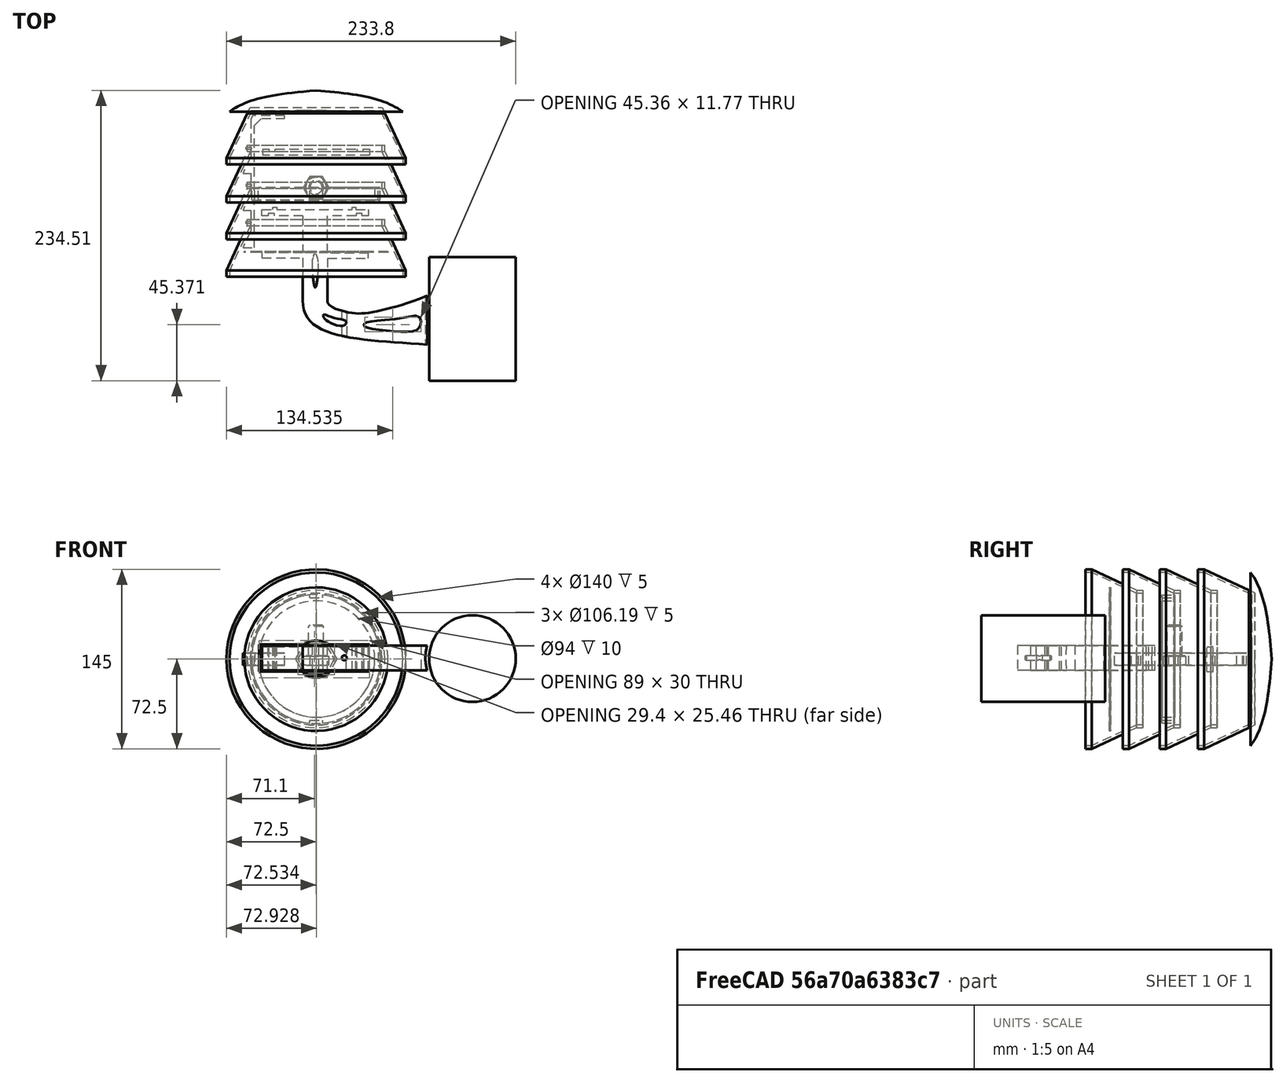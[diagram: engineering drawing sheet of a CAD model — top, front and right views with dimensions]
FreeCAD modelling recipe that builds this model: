
FCSTD DOCUMENT  (FreeCAD 0.21R33771 (Git))
Label: pms7003-external-housing
License: All rights reserved
LicenseURL: http://en.wikipedia.org/wiki/All_rights_reserved
objects: Sketcher::SketchObject×11, Part::Cut×8, Part::Revolution×5, Part::Cylinder×5, Part::Extrusion×5, Part::Box×5, Mesh::Feature×2, App::LinkGroup×2, PartDesign::Body×1, Part::Helix×1, Part::FeaturePython×1, PartDesign::AdditivePipe×1, PartDesign::AdditiveCylinder×1, App::Part×1
note: 46 computed .brp shape members not serialized (recipe doc carries the construction recipe); baked Part::Feature solids carry a one-line shape summary decoded from their .brp

FEATURE [Mesh::Feature] external_v4_case_with_hang_rails  label="external-v4-case-with-hang-rails"
  Placement = pos=(-30.9,-17.3,29) rot=(0,0,1;0rad)
FEATURE [Sketcher::SketchObject] Sketch008
  FullyConstrained = false
  sketch-geometry (8):
    g0: LineSegment StartX=-70 StartY=-1.85789 StartZ=0 EndX=-72.5 EndY=-1.85789 EndZ=0
    g1: LineSegment StartX=-55.5953 StartY=39.3944 StartZ=0 EndX=-55.5953 EndY=44.3944 EndZ=0
    g2: LineSegment StartX=-55.5953 StartY=44.3944 StartZ=0 EndX=-53.0953 EndY=44.3944 EndZ=0
    g3: LineSegment StartX=-53.0953 StartY=39.3944 StartZ=0 EndX=-70 EndY=3.14211 EndZ=0
    g4: LineSegment StartX=-70 StartY=3.14211 StartZ=0 EndX=-70 EndY=-1.85789 EndZ=0
    g5: LineSegment StartX=-72.5 StartY=-1.85789 StartZ=0 EndX=-72.5 EndY=3.14211 EndZ=0
    g6: LineSegment StartX=-72.5 StartY=3.14211 StartZ=0 EndX=-55.5953 EndY=39.3944 EndZ=0
    g7: LineSegment StartX=-53.0953 StartY=44.3944 StartZ=0 EndX=-53.0953 EndY=39.3944 EndZ=0
  constraints (23):
    c: Coincident(g0,g5)
    c: Coincident(g6,g1)
    c: Coincident(g1,g2)
    c: Coincident(g7,g3)
    c: Coincident(g4,g0)
    c: Vertical(g1)
    c: Coincident(g3,g4)
    c: Coincident(g5,g6)
    c: Parallel(g6,g3)
    c: Vertical(g5)
    c: Vertical(g4)
    c: DistanceY(g5,g5) = 5
    c: Distance(g6) = 40
    c: Vertical(g7)
    c: DistanceX(g0,g-1) = 70
    c: Coincident(g7,g2)
    c: DistanceY(g1,g1) = 5
    c: Angle(g-1,g6) = 1.13446
    c: DistanceY(g4,g4) = 5
    c: DistanceY(g7,g7) = 5
    c: Horizontal(g0)
    c: DistanceX(g5,g3) = 2.5
    c: Horizontal(g2)
FEATURE [Part::Revolution] Revolve004  label="ring"
  Angle = 360
  Axis = (0,1,0)
  Base = (0,0,0)
  FaceMakerClass = Part::FaceMakerBullseye
  Placement = pos=(0,-70,0) rot=(0,0,1;0rad)
  Solid = true
  Source = -> Sketch008
  Symmetric = false
FEATURE [Sketcher::SketchObject] Sketch009
  FullyConstrained = false
  sketch-geometry (9):
    g0: LineSegment StartX=-70 StartY=-1.80024 StartZ=0 EndX=-72.5 EndY=-1.80024 EndZ=0
    g1: LineSegment StartX=-52.0979 StartY=41.591 StartZ=0 EndX=-70 EndY=3.19976 EndZ=0
    g2: LineSegment StartX=-70 StartY=3.19976 StartZ=0 EndX=-70 EndY=-1.80024 EndZ=0
    g3: LineSegment StartX=-72.5 StartY=-1.80024 StartZ=0 EndX=-72.5 EndY=3.19976 EndZ=0
    g4: LineSegment StartX=-72.5 StartY=3.19976 StartZ=0 EndX=-55.5953 EndY=39.4521 EndZ=0
    g5: LineSegment StartX=-55.5953 StartY=39.4521 StartZ=0 EndX=-53.3632 EndY=44.091 EndZ=0
    g6: LineSegment StartX=-53.3632 StartY=44.091 StartZ=0 EndX=0 EndY=44.091 EndZ=0
    g7: LineSegment StartX=0 StartY=44.091 StartZ=0 EndX=0 EndY=41.591 EndZ=0
    g8: LineSegment StartX=0 StartY=41.591 StartZ=0 EndX=-52.0979 EndY=41.591 EndZ=0
  constraints (24):
    c: Coincident(g0,g3)
    c: Coincident(g2,g0)
    c: Coincident(g1,g2)
    c: Coincident(g3,g4)
    c: Parallel(g4,g1)
    c: Vertical(g3)
    c: Vertical(g2)
    c: DistanceY(g3,g3) = 5
    c: Distance(g4) = 40
    c: DistanceX(g0,g-1) = 70
    c: Angle(g-1,g4) = 1.13446
    c: DistanceY(g2,g2) = 5
    c: Horizontal(g0)
    c: DistanceX(g3,g1) = 2.5
    c: Coincident(g4,g5)
    c: Coincident(g5,g6)
    c: PointOnObject(g6,g-2)
    c: Horizontal(g6)
    c: Coincident(g6,g7)
    c: PointOnObject(g7,g-2)
    c: Coincident(g8,g1)
    c: Horizontal(g8)
    c: DistanceY(g7,g7) = 2.5
    c: Coincident(g8,g7)
FEATURE [Part::Revolution] Revolve005  label="top"
  Angle = 360
  Axis = (0,1,0)
  Base = (0,0,0)
  FaceMakerClass = Part::FaceMakerBullseye
  Placement = pos=(0,20.7,0) rot=(0,0,1;0rad)
  Solid = true
  Source = -> Sketch009
  Symmetric = false
FEATURE [Part::Cylinder] Cylinder  label="drain pipe"
  Angle = 360
  AttacherType = Attacher::AttachEngine3D
  FirstAngle = 0
  Height = 100
  Placement = pos=(126.3,-156,0.4) rot=(-1,0,0;1.5708rad)
  Radius = 35
  SecondAngle = 0
FEATURE [Sketcher::SketchObject] Sketch
  FullyConstrained = false
  sketch-geometry (112):
    g0: LineSegment StartX=91.0358 StartY=-48.6295 StartZ=0 EndX=101.036 EndY=-48.6295 EndZ=0
    g1: LineSegment StartX=101.036 StartY=-48.6295 StartZ=0 EndX=101.036 EndY=-118.629 EndZ=0
    g2: LineSegment StartX=101.036 StartY=-118.629 StartZ=0 EndX=91.0358 EndY=-118.629 EndZ=0
    g3: LineSegment StartX=9.24219 StartY=-69.33 StartZ=0 EndX=9.24219 EndY=-68.33 EndZ=0
    g4: LineSegment StartX=91.0358 StartY=-106.113 StartZ=0 EndX=91.0358 EndY=-103.552 EndZ=0
    g5: LineSegment StartX=93.0358 StartY=-106.113 StartZ=0 EndX=91.0358 EndY=-106.113 EndZ=0
    g6: LineSegment StartX=93.0358 StartY=-111.113 StartZ=0 EndX=93.0358 EndY=-106.113 EndZ=0
    g7: LineSegment StartX=91.0358 StartY=-118.629 StartZ=0 EndX=91.0358 EndY=-111.113 EndZ=0
    g8: LineSegment StartX=91.0358 StartY=-111.113 StartZ=0 EndX=93.0358 EndY=-111.113 EndZ=0
    g9: LineSegment StartX=91.0358 StartY=-54.3159 StartZ=0 EndX=91.0358 EndY=-48.6295 EndZ=0
    g10: LineSegment StartX=93.7542 StartY=-54.3159 StartZ=0 EndX=91.0358 EndY=-54.3159 EndZ=0
    g11: LineSegment StartX=93.7542 StartY=-59.3159 StartZ=0 EndX=93.7542 EndY=-54.3159 EndZ=0
    g12: LineSegment StartX=91.0358 StartY=-63.2119 StartZ=0 EndX=91.0358 EndY=-59.3159 EndZ=0
    g13: LineSegment StartX=91.0358 StartY=-59.3159 StartZ=0 EndX=93.7542 EndY=-59.3159 EndZ=0
    g14: LineSegment StartX=-43.7578 StartY=0.67 StartZ=0 EndX=-43.7578 EndY=5.67 EndZ=0
    g15: LineSegment StartX=42.2422 StartY=5.67 StartZ=0 EndX=42.2422 EndY=0.67 EndZ=0
    g16: LineSegment StartX=-38.7578 StartY=0.67 StartZ=0 EndX=-43.7578 EndY=0.67 EndZ=0
    g17: LineSegment StartX=-38.7578 StartY=2.67 StartZ=0 EndX=-38.7578 EndY=0.67 EndZ=0
    g18: LineSegment StartX=-33.7578 StartY=2.67 StartZ=0 EndX=-38.7578 EndY=2.67 EndZ=0
    g19: LineSegment StartX=-10.7578 StartY=0.67 StartZ=0 EndX=-33.7578 EndY=0.67 EndZ=0
    g20: LineSegment StartX=-33.7578 StartY=0.67 StartZ=0 EndX=-33.7578 EndY=2.67 EndZ=0
    g21: LineSegment StartX=32.2422 StartY=0.67 StartZ=0 EndX=9.24219 EndY=0.67 EndZ=0
    g22: LineSegment StartX=32.2422 StartY=2.67 StartZ=0 EndX=32.2422 EndY=0.67 EndZ=0
    g23: LineSegment StartX=37.2422 StartY=2.67 StartZ=0 EndX=32.2422 EndY=2.67 EndZ=0
    g24: LineSegment StartX=42.2422 StartY=0.67 StartZ=0 EndX=37.2422 EndY=0.67 EndZ=0
    g25: LineSegment StartX=37.2422 StartY=0.67 StartZ=0 EndX=37.2422 EndY=2.67 EndZ=0
    g26-g29: Circle x4 (B-spline internal-alignment scaffolding for g30; pole/knot coordinates omitted)
    g30: BSplineCurve PolesCount=4 KnotsCount=2 Degree=3 IsPeriodic=0
    g31: GeomPoint X=-10.7578 Y=-67.6904 Z=0
    g32: GeomPoint X=91.0358 Y=-103.552 Z=0
    g33-g39: Circle x7 (B-spline internal-alignment scaffolding for g40; pole/knot coordinates omitted)
    g40: BSplineCurve PolesCount=7 KnotsCount=5 Degree=3 IsPeriodic=0
    g41-g45: GeomPoint x5 (B-spline internal-alignment scaffolding for g40; pole/knot coordinates omitted)
    g46-g55: Circle x10 (B-spline internal-alignment scaffolding for g56; pole/knot coordinates omitted)
    g56: BSplineCurve PolesCount=10 KnotsCount=8 Degree=3 IsPeriodic=0
    g57-g64: GeomPoint x8 (B-spline internal-alignment scaffolding for g56; pole/knot coordinates omitted)
    g65-g70: Circle x6 (B-spline internal-alignment scaffolding for g71; pole/knot coordinates omitted)
    g71: BSplineCurve PolesCount=6 KnotsCount=7 Degree=3 IsPeriodic=1
    g72-g78: GeomPoint x7 (B-spline internal-alignment scaffolding for g71; pole/knot coordinates omitted)
    g79-g84: Circle x6 (B-spline internal-alignment scaffolding for g85; pole/knot coordinates omitted)
    g85: BSplineCurve PolesCount=6 KnotsCount=7 Degree=3 IsPeriodic=1
    g86-g92: GeomPoint x7 (B-spline internal-alignment scaffolding for g85; pole/knot coordinates omitted)
    g93: LineSegment StartX=9.24219 StartY=-33.4521 StartZ=0 EndX=42.2422 EndY=-33.4521 EndZ=0
    g94: LineSegment StartX=42.2422 StartY=-33.4521 StartZ=0 EndX=42.2422 EndY=-29.4521 EndZ=0
    g95: LineSegment StartX=42.2422 StartY=-29.4521 StartZ=0 EndX=9.24219 EndY=-29.4521 EndZ=0
    g96: LineSegment StartX=9.24219 StartY=-29.4521 StartZ=0 EndX=9.24219 EndY=0.67 EndZ=0
    g97: LineSegment StartX=9.24219 StartY=-33.4521 StartZ=0 EndX=9.24219 EndY=-68.33 EndZ=0
    g98: LineSegment StartX=-10.7578 StartY=0.67 StartZ=0 EndX=-10.7578 EndY=-29.2335 EndZ=0
    g99: LineSegment StartX=-10.7578 StartY=-29.2335 StartZ=0 EndX=-43.7578 EndY=-29.2335 EndZ=0
    g100: LineSegment StartX=-43.7578 StartY=-29.2335 StartZ=0 EndX=-43.7578 EndY=-33.2335 EndZ=0
    g101: LineSegment StartX=-43.7578 StartY=-33.2335 StartZ=0 EndX=-10.7578 EndY=-33.2335 EndZ=0
    g102: LineSegment StartX=-10.7578 StartY=-33.2335 StartZ=0 EndX=-10.7578 EndY=-67.6904 EndZ=0
    g103: LineSegment StartX=-43.7578 StartY=5.67 StartZ=0 EndX=-34.8399 EndY=5.67 EndZ=0
    g104: LineSegment StartX=-34.8399 StartY=5.67 StartZ=0 EndX=-34.8399 EndY=7.67 EndZ=0
    g105: LineSegment StartX=-34.8399 StartY=7.67 StartZ=0 EndX=-31.8399 EndY=7.67 EndZ=0
    g106: LineSegment StartX=-31.8399 StartY=7.67 StartZ=0 EndX=-31.8399 EndY=5.67 EndZ=0
    g107: LineSegment StartX=-31.8399 StartY=5.67 StartZ=0 EndX=29.1781 EndY=5.67 EndZ=0
    g108: LineSegment StartX=29.1781 StartY=5.67 StartZ=0 EndX=29.1781 EndY=7.67 EndZ=0
    g109: LineSegment StartX=29.1781 StartY=7.67 StartZ=0 EndX=32.1781 EndY=7.67 EndZ=0
    g110: LineSegment StartX=32.1781 StartY=7.67 StartZ=0 EndX=32.1781 EndY=5.67 EndZ=0
    g111: LineSegment StartX=32.1781 StartY=5.67 StartZ=0 EndX=42.2422 EndY=5.67 EndZ=0
  constraints (152):
    c: Coincident(g9,g0)
    c: Horizontal(g0)
    c: Coincident(g0,g1)
    c: Vertical(g1)
    c: Coincident(g1,g2)
    c: Horizontal(g2)
    c: Coincident(g2,g7)
    c: DistanceX(g0,g0) = 10
    c: DistanceX(g2,g2) = 10
    c: Vertical(g3)
    c: DistanceY(g1,g1) = 70
    c: Coincident(g5,g4)
    c: Vertical(g4)
    c: Coincident(g6,g5)
    c: Coincident(g8,g6)
    c: Vertical(g6)
    c: Coincident(g7,g8)
    c: Vertical(g7)
    c: Horizontal(g5)
    c: Horizontal(g8)
    c: DistanceY(g6,g6) = 5
    c: Coincident(g10,g9)
    c: Vertical(g9)
    c: Coincident(g11,g10)
    c: Coincident(g13,g11)
    c: Vertical(g11)
    c: Coincident(g12,g13)
    c: Vertical(g12)
    c: DistanceY(g11,g11) = 5
    c: Horizontal(g10)
    c: Horizontal(g13)
    c: DistanceX(g5,g5) = 2
    c: DistanceX(g4,g1) = 10
    c: DistanceX(g12,g0) = 10
    c: DistanceY(g3,g96) = 70
    c: Coincident(g98,g19)
    c: Coincident(g16,g14)
    c: Vertical(g14)
    c: Coincident(g14,g103)
    c: Coincident(g111,g15)
    c: Coincident(g15,g24)
    c: Coincident(g21,g96)
    c: Vertical(g15)
    c: Coincident(g17,g16)
    c: Horizontal(g16)
    c: Coincident(g18,g17)
    c: Coincident(g20,g18)
    c: Horizontal(g18)
    c: Coincident(g19,g20)
    c: Horizontal(g19)
    c: Vertical(g17)
    c: Vertical(g20)
    c: DistanceX(g18,g18) = 5
    c: DistanceY(g20,g20) = 2
    c: Coincident(g22,g21)
    c: Horizontal(g21)
    c: Coincident(g23,g22)
    c: Coincident(g25,g23)
    c: Horizontal(g23)
    c: Coincident(g24,g25)
    c: Horizontal(g24)
    c: Vertical(g22)
    c: Vertical(g25)
    c: DistanceX(g23,g23) = 5
    c: DistanceY(g25,g25) = 2
    c: DistanceY(g96,g111) = 5
    c: DistanceY(g96,g98) = 0
    c: DistanceX(g98,g96) = 20
    c: DistanceY(g22,g22) = 2
    c: DistanceY(g17,g17) = 2
    c: DistanceX(g19,g98) = 23
    c: DistanceX(g96,g21) = 23
    c: DistanceX(g96,g111) = 33
    c: DistanceX(g14,g98) = 33
    c: Weight(g26) = 1
    c: Coincident(g30,g102)
    c: Equal(g26,g27)
    c: Equal(g26,g28)
    c: Equal(g26,g29)
    c: Coincident(g30,g4)
    c: InternalAlignment(g26-g29 -> g30) x4
    c: InternalAlignment(g31,g30)
    c: InternalAlignment(g32,g30)
    c: Weight(g33) = 1
    c: Coincident(g40,g3)
    c: Equal(g33, g34-g39) x6
    c: Coincident(g40,g12)
    c: InternalAlignment(g33-g39 -> g40) x7
    c: InternalAlignment(g41-g45 -> g40) x5
    c: Weight(g46) = 1
    c: Equal(g46, g47-g55) x9
    c: Coincident(g56,g46)
    c: InternalAlignment(g46-g55 -> g56) x10
    c: InternalAlignment(g57-g64 -> g56) x8
    c: Weight(g65) = 1
    c: Equal(g65, g66-g70) x5
    c: InternalAlignment(g65-g70 -> g71) x6
    c: InternalAlignment(g72-g78 -> g71) x7
    c: Weight(g79) = 1
    c: Equal(g79, g80-g84) x5
    c: InternalAlignment(g79-g84 -> g85) x6
    c: InternalAlignment(g86-g92 -> g85) x7
    c: PointOnObject(g93,g3)
    c: Horizontal(g93)
    c: Coincident(g93,g94)
    c: Vertical(g94)
    c: Coincident(g94,g95)
    c: Horizontal(g95)
    c: PointOnObject(g3,g33)
    c: Coincident(g96,g95)
    c: Coincident(g97,g93)
    c: Coincident(g97,g3)
    c: Coincident(g98,g99)
    c: Vertical(g98)
    c: Coincident(g99,g100)
    c: Coincident(g100,g101)
    c: Coincident(g101,g102)
    c: Vertical(g102)
    c: Vertical(g100)
    c: Horizontal(g99)
    c: Horizontal(g101)
    c: DistanceY(g94,g94) = 4
    c: DistanceY(g100,g100) = 4
    c: DistanceX(g95,g95) = 33
    c: DistanceX(g99,g99) = 33
    c: Vertical(g96)
    c: Equal(g99,g101)
    c: Equal(g95,g93)
    c: Coincident(g103,g104)
    c: Horizontal(g103)
    c: Coincident(g104,g105)
    c: Coincident(g105,g106)
    c: Horizontal(g105)
    c: Coincident(g106,g107)
    c: Vertical(g104)
    c: Vertical(g106)
    c: DistanceY(g106,g106) = 2
    c: DistanceY(g106,g103) = 0
    c: DistanceX(g105,g105) = 3
    c: DistanceY(g-1,g15) = 5.67
    c: Coincident(g107,g108)
    c: Horizontal(g107)
    c: Coincident(g108,g109)
    c: Coincident(g109,g110)
    c: Horizontal(g109)
    c: Coincident(g110,g111)
    c: Horizontal(g111)
    c: Vertical(g108)
    c: Vertical(g110)
    c: DistanceY(g108,g108) = 2
    c: DistanceX(g109,g109) = 3
    c: DistanceY(g107,g110) = 0
FEATURE [Part::Extrusion] Extrude  label="support"
  Base = -> Sketch
  Dir = (0,0,1)
  DirMode = 2
  FaceMakerClass = Part::FaceMakerBullseye
  LengthFwd = 20
  LengthRev = 0
  Placement = pos=(0,-23.5,-20) rot=(0,0,1;0rad)
  Solid = true
  Symmetric = false
FEATURE [Part::Cylinder] Cylinder001  label="drain pipe001"
  Angle = 360
  AttacherType = Attacher::AttachEngine3D
  FirstAngle = 0
  Height = 100
  Placement = pos=(123.3,-155.1,-10) rot=(-1,0,0;1.5708rad)
  Radius = 35
  SecondAngle = 0
FEATURE [Part::Cut] Cut  label="bracket"
  Base = -> Extrude
  Tool = -> Cylinder001
FEATURE [PartDesign::Body] Body
  Origin = -> Origin001
FEATURE [Part::Helix] Helix
  Angle = 0
  AttacherType = Attacher::AttachEngine3D
  Height = 25
  LocalCoord = 0
  Pitch = 5
  Radius = 7.5
  SegmentLength = 0
  Style = 1
FEATURE [Part::FeaturePython] Screw  label="M12x25-Screw"  # Fasteners workbench fastener (typed FeaturePython)
  Placement = pos=(0,0,2.5) rot=(1,0,0;3.14159rad)
  diameter = 11
  invert = false
  leftHanded = false
  length = 0
  lengthCustom = 25
  matchOuter = false
  offset = 0
  thread = false
  type = 32
FEATURE [Sketcher::SketchObject] Sketch010
  FullyConstrained = true
  MapMode = 5
  Placement = pos=(0,0,0) rot=(1,0,0;1.5708rad)
  sketch-geometry (4):
    g0: LineSegment StartX=7.5 StartY=2.4 StartZ=0 EndX=7.5 EndY=0.1 EndZ=0
    g1: LineSegment StartX=7.5 StartY=0.1 StartZ=0 EndX=9 EndY=0.487926 EndZ=0
    g2: LineSegment StartX=9 StartY=0.487926 StartZ=0 EndX=9 EndY=2.01207 EndZ=0
    g3: LineSegment StartX=9 StartY=2.01207 StartZ=0 EndX=7.5 EndY=2.4 EndZ=0
  constraints (12):
    c: Vertical(g0)
    c: Coincident(g0,g1)
    c: Coincident(g1,g2)
    c: Coincident(g2,g3)
    c: Coincident(g3,g0)
    c: DistanceY(g0,g0) = 2.3
    c: DistanceX(g3,g3) = 1.5
    c: DistanceX(g-1,g0) = 7.5
    c: Vertical(g2)
    c: DistanceY(g-1,g0) = 0.1
    c: Angle(g0,g3) = 1.31772
    c: Angle(g1,g0) = 1.31772
FEATURE [PartDesign::AdditivePipe] AdditivePipe
  AuxilleryCurvelinear = true
  AuxillerySpineTangent = false
  Binormal = (0,0,0)
  Mode = 2
  Placement = pos=(0,0,0) rot=(1,0,0;1.5708rad)
  Profile = -> Sketch010
  Spine = -> Helix
  SpineTangent = false
  Transformation = 0
  Transition = 0
FEATURE [PartDesign::AdditiveCylinder] Cylinder002
  Angle = 360
  AttacherType = Attacher::AttachEngine3D
  BaseFeature = -> AdditivePipe
  FirstAngle = 0
  Height = 27.5
  Radius = 7.5
  SecondAngle = 0
FEATURE [App::Part] Part001  label="Bolt"
  Group = -> [Sketch010,Cylinder002,AdditivePipe,Helix,Body,Screw]
  Origin = -> Origin002
  Placement = pos=(0,31.5,0) rot=(1,0,0;4.71239rad)
FEATURE [Sketcher::SketchObject] Sketch011
  FullyConstrained = false
  sketch-geometry (12):
    g0: LineSegment StartX=-43 StartY=26.1919 StartZ=0 EndX=-43 EndY=31.1919 EndZ=0
    g1: LineSegment StartX=43 StartY=31.1919 StartZ=0 EndX=43 EndY=26.1919 EndZ=0
    g2: LineSegment StartX=43 StartY=26.1919 StartZ=0 EndX=-43 EndY=26.1919 EndZ=0
    g3: LineSegment StartX=-43 StartY=31.1919 StartZ=0 EndX=-38 EndY=31.1919 EndZ=0
    g4: LineSegment StartX=-38 StartY=31.1919 StartZ=0 EndX=-38 EndY=29.1919 EndZ=0
    g5: LineSegment StartX=-38 StartY=29.1919 StartZ=0 EndX=-33 EndY=29.1919 EndZ=0
    g6: LineSegment StartX=-33 StartY=29.1919 StartZ=0 EndX=-33 EndY=31.1919 EndZ=0
    g7: LineSegment StartX=-33 StartY=31.1919 StartZ=0 EndX=33 EndY=31.1919 EndZ=0
    g8: LineSegment StartX=33 StartY=31.1919 StartZ=0 EndX=33 EndY=29.1919 EndZ=0
    g9: LineSegment StartX=33 StartY=29.1919 StartZ=0 EndX=38 EndY=29.1919 EndZ=0
    g10: LineSegment StartX=38 StartY=29.1919 StartZ=0 EndX=38 EndY=31.1919 EndZ=0
    g11: LineSegment StartX=38 StartY=31.1919 StartZ=0 EndX=43 EndY=31.1919 EndZ=0
  constraints (35):
    c: Vertical(g0)
    c: Vertical(g1)
    c: Horizontal(g2)
    c: DistanceY(g2,g1) = 5
    c: Coincident(g0,g3)
    c: Coincident(g1,g11)
    c: Coincident(g3,g4)
    c: Horizontal(g3)
    c: Coincident(g4,g5)
    c: Coincident(g5,g6)
    c: Horizontal(g5)
    c: Coincident(g6,g7)
    c: DistanceX(g5,g5) = 5
    c: Vertical(g4)
    c: Vertical(g6)
    c: Coincident(g7,g8)
    c: Horizontal(g7)
    c: Coincident(g8,g9)
    c: Coincident(g9,g10)
    c: Horizontal(g9)
    c: Coincident(g10,g11)
    c: Horizontal(g11)
    c: DistanceX(g9,g9) = 5
    c: Vertical(g8)
    c: Vertical(g10)
    c: DistanceX(g6,g-1) = 33
    c: DistanceX(g-1,g7) = 33
    c: DistanceY(g4,g4) = 2
    c: DistanceY(g6,g6) = 2
    c: Coincident(g2,g0)
    c: Coincident(g1,g2)
    c: DistanceY(g8,g8) = 2
    c: DistanceY(g10,g10) = 2
    c: DistanceX(g3,g3) = 5
    c: DistanceX(g11,g11) = 5
FEATURE [Part::Extrusion] Extrude001
  Base = -> Sketch011
  Dir = (0,0,1)
  DirMode = 2
  FaceMakerClass = Part::FaceMakerBullseye
  LengthFwd = 20
  LengthRev = 0
  Placement = pos=(0,0,-10) rot=(1,0,0;0rad)
  Solid = true
  Symmetric = false
FEATURE [Part::Cylinder] Cylinder003  label="Cylinder"
  Angle = 360
  AttacherType = Attacher::AttachEngine3D
  FirstAngle = 0
  Height = 34
  Placement = pos=(22.8,-95.5,-10) rot=(1,0,0;1.5708rad)
  Radius = 2
  SecondAngle = 0
FEATURE [Part::Cut] Cut001  label="bracket001"
  Base = -> Cut
  Placement = pos=(0,0,11) rot=(0,0,1;0rad)
  Tool = -> Cylinder003
FEATURE [Sketcher::SketchObject] Sketch012
  FullyConstrained = false
  sketch-geometry (8):
    g0: LineSegment StartX=-70 StartY=-1.85789 StartZ=0 EndX=-72.5 EndY=-1.85789 EndZ=0
    g1: LineSegment StartX=-55.5953 StartY=39.3944 StartZ=0 EndX=-55.5953 EndY=44.3944 EndZ=0
    g2: LineSegment StartX=-55.5953 StartY=44.3944 StartZ=0 EndX=-53.0953 EndY=44.3944 EndZ=0
    g3: LineSegment StartX=-53.0953 StartY=39.3944 StartZ=0 EndX=-70 EndY=3.14211 EndZ=0
    g4: LineSegment StartX=-70 StartY=3.14211 StartZ=0 EndX=-70 EndY=-1.85789 EndZ=0
    g5: LineSegment StartX=-72.5 StartY=-1.85789 StartZ=0 EndX=-72.5 EndY=3.14211 EndZ=0
    g6: LineSegment StartX=-72.5 StartY=3.14211 StartZ=0 EndX=-55.5953 EndY=39.3944 EndZ=0
    g7: LineSegment StartX=-53.0953 StartY=44.3944 StartZ=0 EndX=-53.0953 EndY=39.3944 EndZ=0
  constraints (23):
    c: Coincident(g0,g5)
    c: Coincident(g6,g1)
    c: Coincident(g1,g2)
    c: Coincident(g7,g3)
    c: Coincident(g4,g0)
    c: Vertical(g1)
    c: Coincident(g3,g4)
    c: Coincident(g5,g6)
    c: Parallel(g6,g3)
    c: Vertical(g5)
    c: Vertical(g4)
    c: DistanceY(g5,g5) = 5
    c: Distance(g6) = 40
    c: Vertical(g7)
    c: DistanceX(g0,g-1) = 70
    c: Coincident(g7,g2)
    c: DistanceY(g1,g1) = 5
    c: Angle(g-1,g6) = 1.13446
    c: DistanceY(g4,g4) = 5
    c: DistanceY(g7,g7) = 5
    c: Horizontal(g0)
    c: DistanceX(g5,g3) = 2.5
    c: Horizontal(g2)
FEATURE [Part::Revolution] Revolve006  label="ring001"
  Angle = 360
  Axis = (0,1,0)
  Base = (0,0,0)
  FaceMakerClass = Part::FaceMakerBullseye
  Placement = pos=(0,-40,0) rot=(0,0,1;0rad)
  Solid = true
  Source = -> Sketch012
  Symmetric = false
FEATURE [Sketcher::SketchObject] Sketch013
  FullyConstrained = false
  sketch-geometry (8):
    g0: LineSegment StartX=-70 StartY=-1.85789 StartZ=0 EndX=-72.5 EndY=-1.85789 EndZ=0
    g1: LineSegment StartX=-55.5953 StartY=39.3944 StartZ=0 EndX=-55.5953 EndY=44.3944 EndZ=0
    g2: LineSegment StartX=-55.5953 StartY=44.3944 StartZ=0 EndX=-53.0953 EndY=44.3944 EndZ=0
    g3: LineSegment StartX=-53.0953 StartY=39.3944 StartZ=0 EndX=-70 EndY=3.14211 EndZ=0
    g4: LineSegment StartX=-70 StartY=3.14211 StartZ=0 EndX=-70 EndY=-1.85789 EndZ=0
    g5: LineSegment StartX=-72.5 StartY=-1.85789 StartZ=0 EndX=-72.5 EndY=3.14211 EndZ=0
    g6: LineSegment StartX=-72.5 StartY=3.14211 StartZ=0 EndX=-55.5953 EndY=39.3944 EndZ=0
    g7: LineSegment StartX=-53.0953 StartY=44.3944 StartZ=0 EndX=-53.0953 EndY=39.3944 EndZ=0
  constraints (23):
    c: Coincident(g0,g5)
    c: Coincident(g6,g1)
    c: Coincident(g1,g2)
    c: Coincident(g7,g3)
    c: Coincident(g4,g0)
    c: Vertical(g1)
    c: Coincident(g3,g4)
    c: Coincident(g5,g6)
    c: Parallel(g6,g3)
    c: Vertical(g5)
    c: Vertical(g4)
    c: DistanceY(g5,g5) = 5
    c: Distance(g6) = 40
    c: Vertical(g7)
    c: DistanceX(g0,g-1) = 70
    c: Coincident(g7,g2)
    c: DistanceY(g1,g1) = 5
    c: Angle(g-1,g6) = 1.13446
    c: DistanceY(g4,g4) = 5
    c: DistanceY(g7,g7) = 5
    c: Horizontal(g0)
    c: DistanceX(g5,g3) = 2.5
    c: Horizontal(g2)
FEATURE [Part::Revolution] Revolve007  label="ring002"
  Angle = 360
  Axis = (0,1,0)
  Base = (0,0,0)
  FaceMakerClass = Part::FaceMakerBullseye
  Placement = pos=(0,-10,0) rot=(0,0,1;0rad)
  Solid = true
  Source = -> Sketch013
  Symmetric = false
FEATURE [App::LinkGroup] LinkGroup001  label="top bolt"
  ElementList = -> [Extrude001,Part001]
  LinkMode = 0
FEATURE [Part::Cylinder] Cylinder004
  Angle = 360
  AttacherType = Attacher::AttachEngine3D
  FirstAngle = 0
  Height = 0.84
  Placement = pos=(0,-49.6,0) rot=(1,0,0;1.5708rad)
  Radius = 58
  SecondAngle = 0
FEATURE [Part::Box] Box  label="Cube"
  AttacherType = Attacher::AttachEngine3D
  Height = 22
  Length = 89
  Placement = pos=(-45.9,-59.6,-10) rot=(0,0,1;0rad)
  Width = 17
FEATURE [Sketcher::SketchObject] Sketch014
  FullyConstrained = false
  sketch-geometry (27):
    g0: LineSegment StartX=-37.4711 StartY=61.97 StartZ=0 EndX=-63.4364 EndY=61.97 EndZ=0
    g1: LineSegment StartX=-64.8 StartY=29.1149 StartZ=0 EndX=-71.1393 EndY=15.5203 EndZ=0
    g2: LineSegment StartX=-71.1393 StartY=15.5203 StartZ=0 EndX=-64.8 EndY=15.5203 EndZ=0
    g3: LineSegment StartX=-64.8 StartY=15.5203 StartZ=0 EndX=-64.8 EndY=-0.866024 EndZ=0
    g4: LineSegment StartX=-64.8 StartY=-0.866024 StartZ=0 EndX=-71.1393 EndY=-14.4606 EndZ=0
    g5: LineSegment StartX=-71.1393 StartY=-14.4606 StartZ=0 EndX=-64.8 EndY=-14.4606 EndZ=0
    g6: LineSegment StartX=-64.8 StartY=-14.4606 StartZ=0 EndX=-64.8 EndY=-30.8823 EndZ=0
    g7: LineSegment StartX=-64.8 StartY=-30.8823 StartZ=0 EndX=-71.1393 EndY=-44.4769 EndZ=0
    g8: LineSegment StartX=-71.1393 StartY=-44.4769 StartZ=0 EndX=-61.8 EndY=-44.4769 EndZ=0
    g9: LineSegment StartX=-37.4711 StartY=59.97 StartZ=0 EndX=-37.4711 EndY=61.97 EndZ=0
    g10: LineSegment StartX=-64.8 StartY=59.0457 StartZ=0 EndX=-64.8 EndY=29.1149 EndZ=0
    g11: LineSegment StartX=-63.4364 StartY=61.97 StartZ=0 EndX=-64.8 EndY=59.0457 EndZ=0
    g12: LineSegment StartX=-61.8 StartY=-44.4769 StartZ=0 EndX=-61.8 EndY=54.1731 EndZ=0
    g13: LineSegment StartX=-61.8 StartY=54.1731 StartZ=0 EndX=-56.0031 EndY=59.97 EndZ=0
    g14: LineSegment StartX=-56.0031 StartY=59.97 StartZ=0 EndX=-37.4711 EndY=59.97 EndZ=0
    g15: LineSegment StartX=-68.4456 StartY=36.8589 StartZ=0 EndX=-64.4456 EndY=36.8589 EndZ=0
    g16: LineSegment StartX=-64.4456 StartY=36.8589 StartZ=0 EndX=-64.4456 EndY=34.8589 EndZ=0
    g17: LineSegment StartX=-64.4456 StartY=34.8589 StartZ=0 EndX=-68.4456 EndY=34.8589 EndZ=0
    g18: LineSegment StartX=-68.4456 StartY=34.8589 StartZ=0 EndX=-68.4456 EndY=36.8589 EndZ=0
    g19: LineSegment StartX=-68.3558 StartY=6.76093 StartZ=0 EndX=-64.3558 EndY=6.76093 EndZ=0
    g20: LineSegment StartX=-64.3558 StartY=6.76093 StartZ=0 EndX=-64.3558 EndY=4.76093 EndZ=0
    g21: LineSegment StartX=-64.3558 StartY=4.76093 StartZ=0 EndX=-68.3558 EndY=4.76093 EndZ=0
    g22: LineSegment StartX=-68.3558 StartY=4.76093 StartZ=0 EndX=-68.3558 EndY=6.76093 EndZ=0
    g23: LineSegment StartX=-68.6426 StartY=-23.2919 StartZ=0 EndX=-64.6426 EndY=-23.2919 EndZ=0
    g24: LineSegment StartX=-64.6426 StartY=-23.2919 StartZ=0 EndX=-64.6426 EndY=-25.2919 EndZ=0
    g25: LineSegment StartX=-64.6426 StartY=-25.2919 StartZ=0 EndX=-68.6426 EndY=-25.2919 EndZ=0
    g26: LineSegment StartX=-68.6426 StartY=-25.2919 StartZ=0 EndX=-68.6426 EndY=-23.2919 EndZ=0
  constraints (69):
    c: Horizontal(g0)
    c: Coincident(g1,g2)
    c: Coincident(g2,g3)
    c: Vertical(g3)
    c: Coincident(g3,g4)
    c: Coincident(g4,g5)
    c: Coincident(g5,g6)
    c: Vertical(g6)
    c: Coincident(g6,g7)
    c: Coincident(g7,g8)
    c: Coincident(g8,g12)
    c: Coincident(g14,g9)
    c: Coincident(g9,g0)
    c: Horizontal(g2)
    c: Horizontal(g5)
    c: Horizontal(g8)
    c: Vertical(g10)
    c: Angle(g8,g7) = 1.13446
    c: Angle(g5,g4) = 1.13446
    c: Angle(g2,g1) = 1.13446
    c: Distance(g4) = 15
    c: Distance(g1) = 15
    c: Distance(g7) = 15
    c: DistanceY(g13,g0) = 2
    c: Vertical(g9)
    c: Coincident(g10,g1)
    c: DistanceX(g5,g3) = 0
    c: DistanceX(g2,g1) = 0
    c: Coincident(g11,g0)
    c: Coincident(g11,g10)
    c: Angle(g10,g11) = 2.70526
    c: DistanceY(g-1,g14) = 59.97
    c: Coincident(g12,g13)
    c: Vertical(g12)
    c: Horizontal(g14)
    c: Coincident(g13,g14)
    c: DistanceX(g10,g12) = 3
    c: DistanceX(g1,g-1) = 64.8
    c: Angle(g12,g13) = 2.35619
    c: Coincident(g15,g16)
    c: Coincident(g16,g17)
    c: Coincident(g17,g18)
    c: Coincident(g18,g15)
    c: Horizontal(g15)
    c: Horizontal(g17)
    c: Vertical(g16)
    c: Vertical(g18)
    c: DistanceY(g18,g18) = 2
    c: DistanceX(g15,g15) = 4
    c: Coincident(g19,g20)
    c: Coincident(g20,g21)
    c: Coincident(g21,g22)
    c: Coincident(g22,g19)
    c: Horizontal(g19)
    c: Horizontal(g21)
    c: Vertical(g20)
    c: Vertical(g22)
    c: DistanceY(g22,g22) = 2
    c: DistanceX(g19,g19) = 4
    c: Coincident(g23,g24)
    c: Coincident(g24,g25)
    c: Coincident(g25,g26)
    c: Coincident(g26,g23)
    c: Horizontal(g23)
    c: Horizontal(g25)
    c: Vertical(g24)
    c: Vertical(g26)
    c: DistanceY(g26,g26) = 2
    c: DistanceX(g23,g23) = 4
FEATURE [Part::Extrusion] Extrude002  label="brace"
  Base = -> Sketch014
  Dir = (0,0,1)
  DirMode = 2
  FaceMakerClass = Part::FaceMakerBullseye
  LengthFwd = 10
  LengthRev = 0
  Placement = pos=(12,-3.9,-5) rot=(0,0,1;0rad)
  Solid = true
  Symmetric = false
FEATURE [Part::Cylinder] Cylinder005
  Angle = 360
  AttacherType = Attacher::AttachEngine3D
  FirstAngle = 0
  Height = 17.84
  Placement = pos=(0,-42.6,0) rot=(1,0,0;1.5708rad)
  Radius = 15
  SecondAngle = 0
FEATURE [Part::Cut] Cut002
  Base = -> Cylinder004
  Tool = -> Box
FEATURE [Part::Cut] Cut003  label="base"
  Base = -> Cut002
  Placement = pos=(0,-2,0) rot=(0,0,1;0rad)
  Tool = -> Cylinder005
FEATURE [Mesh::Feature] threadv5_nut  label="threadv5-nut"
  Placement = pos=(-58,59,0) rot=(-1,0,0;4.71239rad)
FEATURE [Sketcher::SketchObject] Sketch015
  FullyConstrained = false
  Placement = pos=(0,0,0) rot=(1,0,0;1.5708rad)
  sketch-geometry (12):
    g0: LineSegment StartX=7.3838 StartY=12.7306 StartZ=0 EndX=14.7338 EndY=0 EndZ=0
    g1: LineSegment StartX=14.7338 StartY=0 StartZ=0 EndX=7.3838 EndY=-12.7306 EndZ=0
    g2: LineSegment StartX=7.3838 StartY=-12.7306 StartZ=0 EndX=-7.3162 EndY=-12.7306 EndZ=0
    g3: LineSegment StartX=-7.3162 StartY=-12.7306 StartZ=0 EndX=-14.6662 EndY=0 EndZ=0
    g4: LineSegment StartX=-14.6662 StartY=0 StartZ=0 EndX=-7.3162 EndY=12.7306 EndZ=0
    g5: LineSegment StartX=8.3838 StartY=14.4626 StartZ=0 EndX=16.7338 EndY=0 EndZ=0
    g6: LineSegment StartX=16.7338 StartY=0 StartZ=0 EndX=8.3838 EndY=-14.4626 EndZ=0
    g7: LineSegment StartX=8.3838 StartY=-14.4626 StartZ=0 EndX=-8.3162 EndY=-14.4626 EndZ=0
    g8: LineSegment StartX=-8.3162 StartY=-14.4626 StartZ=0 EndX=-16.6662 EndY=0 EndZ=0
    g9: LineSegment StartX=-16.6662 StartY=0 StartZ=0 EndX=-8.3162 EndY=14.4626 EndZ=0
    g10: LineSegment StartX=-7.3162 StartY=12.7306 StartZ=0 EndX=7.3838 EndY=12.7306 EndZ=0
    g11: LineSegment StartX=-8.3162 StartY=14.4626 StartZ=0 EndX=8.3838 EndY=14.4626 EndZ=0
  constraints (35):
    c: Coincident(g0,g1)
    c: Coincident(g1,g2)
    c: Horizontal(g2)
    c: Coincident(g2,g3)
    c: Coincident(g3,g4)
    c: Coincident(g5,g6)
    c: Coincident(g6,g7)
    c: Horizontal(g7)
    c: Coincident(g7,g8)
    c: Coincident(g8,g9)
    c: Angle(g0,g1) = 2.0944
    c: Angle(g8,g9) = 2.0944
    c: Angle(g6,g7) = 2.0944
    c: Angle(g3,g4) = 2.0944
    c: DistanceX(g8,g3) = 2
    c: DistanceX(g0,g5) = 2
    c: DistanceY(g5,g0) = 0
    c: DistanceY(g3,g8) = 0
    c: Distance(g4,g9) = 2
    c: Distance(g2,g7) = 2
    c: Coincident(g10,g4)
    c: Coincident(g10,g0)
    c: Horizontal(g10)
    c: Coincident(g11,g9)
    c: Coincident(g11,g5)
    c: Horizontal(g11)
    c: DistanceY(g3,g-1) = 0
    c: DistanceY(g-1,g0) = 0
    c: Distance(g0,g5) = 2
    c: Distance(g1,g6) = 2
    c: Angle(g10,g0) = 2.0944
    c: Angle(g4,g10) = 2.0944
    c: DistanceX(g10,g10) = 14.7
    c: DistanceX(g2,g2) = 14.7
    c: Distance(g4) = 14.7
FEATURE [Part::Extrusion] Extrude003
  Base = -> Sketch015
  Dir = (0,-1,2e-16)
  DirMode = 2
  FaceMakerClass = Part::FaceMakerBullseye
  LengthFwd = 2
  LengthRev = 0
  Placement = pos=(0,62.2,0) rot=(0,0,1;0rad)
  Solid = true
  Symmetric = false
FEATURE [App::LinkGroup] LinkGroup  label="lamp shade"
  ElementList = -> [Revolve005,Revolve004,Revolve006,Revolve007,Extrude003]
  LinkMode = 0
  Placement = pos=(0,-3.6,0) rot=(0,0,1;0rad)
FEATURE [Sketcher::SketchObject] Sketch016
  FullyConstrained = false
  sketch-geometry (9):
    g0: LineSegment StartX=0 StartY=61.2276 StartZ=0 EndX=-70 EndY=61.2276 EndZ=0
    g1: LineSegment StartX=0 StartY=61.2276 StartZ=0 EndX=0 EndY=78.5122 EndZ=0
    g2-g5: Circle x4 (B-spline internal-alignment scaffolding for g6; pole/knot coordinates omitted)
    g6: BSplineCurve PolesCount=4 KnotsCount=2 Degree=3 IsPeriodic=0
    g7: GeomPoint X=-70 Y=61.2276 Z=0
    g8: GeomPoint X=0 Y=78.5122 Z=0
  constraints (14):
    c: PointOnObject(g0,g-2)
    c: Horizontal(g0)
    c: Coincident(g1,g0)
    c: PointOnObject(g1,g-2)
    c: Weight(g2) = 1
    c: Coincident(g6,g0)
    c: Equal(g2,g3)
    c: Equal(g2,g4)
    c: Equal(g2,g5)
    c: InternalAlignment(g2-g5 -> g6) x4
    c: InternalAlignment(g7,g6)
    c: InternalAlignment(g8,g6)
    c: Coincident(g6,g1)
    c: DistanceX(g0,g0) = 70
FEATURE [Part::Revolution] Revolve  label="top cap"
  Angle = 360
  Axis = (0,1,0)
  Base = (0,0,0)
  FaceMakerClass = Part::FaceMakerBullseye
  Solid = true
  Source = -> Sketch016
  Symmetric = false
FEATURE [Sketcher::SketchObject] Sketch017
  FullyConstrained = false
  Placement = pos=(0,0,0) rot=(1,0,0;1.5708rad)
  sketch-geometry (2):
    g0: Circle CenterX=0 CenterY=0 CenterZ=0 NormalX=0 NormalY=0 NormalZ=1 AngleXU=0 Radius=52
    g1: Circle CenterX=0.427685 CenterY=0 CenterZ=0 NormalX=0 NormalY=0 NormalZ=1 AngleXU=0 Radius=47
  constraints (4):
    c: Coincident(g0,g-1)
    c: Radius(g0) = 52
    c: PointOnObject(g1,g-1)
    c: Radius(g1) = 47
FEATURE [Part::Extrusion] Extrude004  label="jig"
  Base = -> Sketch017
  Dir = (0,-1,-2e-16)
  DirMode = 2
  FaceMakerClass = Part::FaceMakerBullseye
  LengthFwd = 10
  LengthRev = 0
  Solid = true
  Symmetric = false
FEATURE [Part::Box] Box001  label="Cube001"
  AttacherType = Attacher::AttachEngine3D
  Height = 10.5
  Length = 10
  Placement = pos=(-59.5,-12,-5.25) rot=(0,0,1;0rad)
  Width = 15
FEATURE [Part::Cut] Cut004
  Base = -> Extrude004
  Tool = -> Box001
FEATURE [Part::Box] Box002  label="Cube002"
  AttacherType = Attacher::AttachEngine3D
  Height = 10.5
  Length = 10
  Placement = pos=(50,-12,-5.35) rot=(0,0,1;0rad)
  Width = 15
FEATURE [Part::Box] Box003  label="Cube003"
  AttacherType = Attacher::AttachEngine3D
  Height = 10.5
  Length = 10
  Placement = pos=(5.5,-12,-59.5) rot=(0,1,0;-1.5708rad)
  Width = 15
FEATURE [Part::Box] Box004  label="Cube004"
  AttacherType = Attacher::AttachEngine3D
  Height = 10.5
  Length = 10
  Placement = pos=(5.5,-12,49.5) rot=(0,-1,0;1.5708rad)
  Width = 15
FEATURE [Part::Cut] Cut005
  Base = -> Cut004
  Tool = -> Box002
FEATURE [Part::Cut] Cut006
  Base = -> Cut005
  Tool = -> Box003
FEATURE [Part::Cut] Cut007  label="brace jig"
  Base = -> Cut006
  Tool = -> Box004
